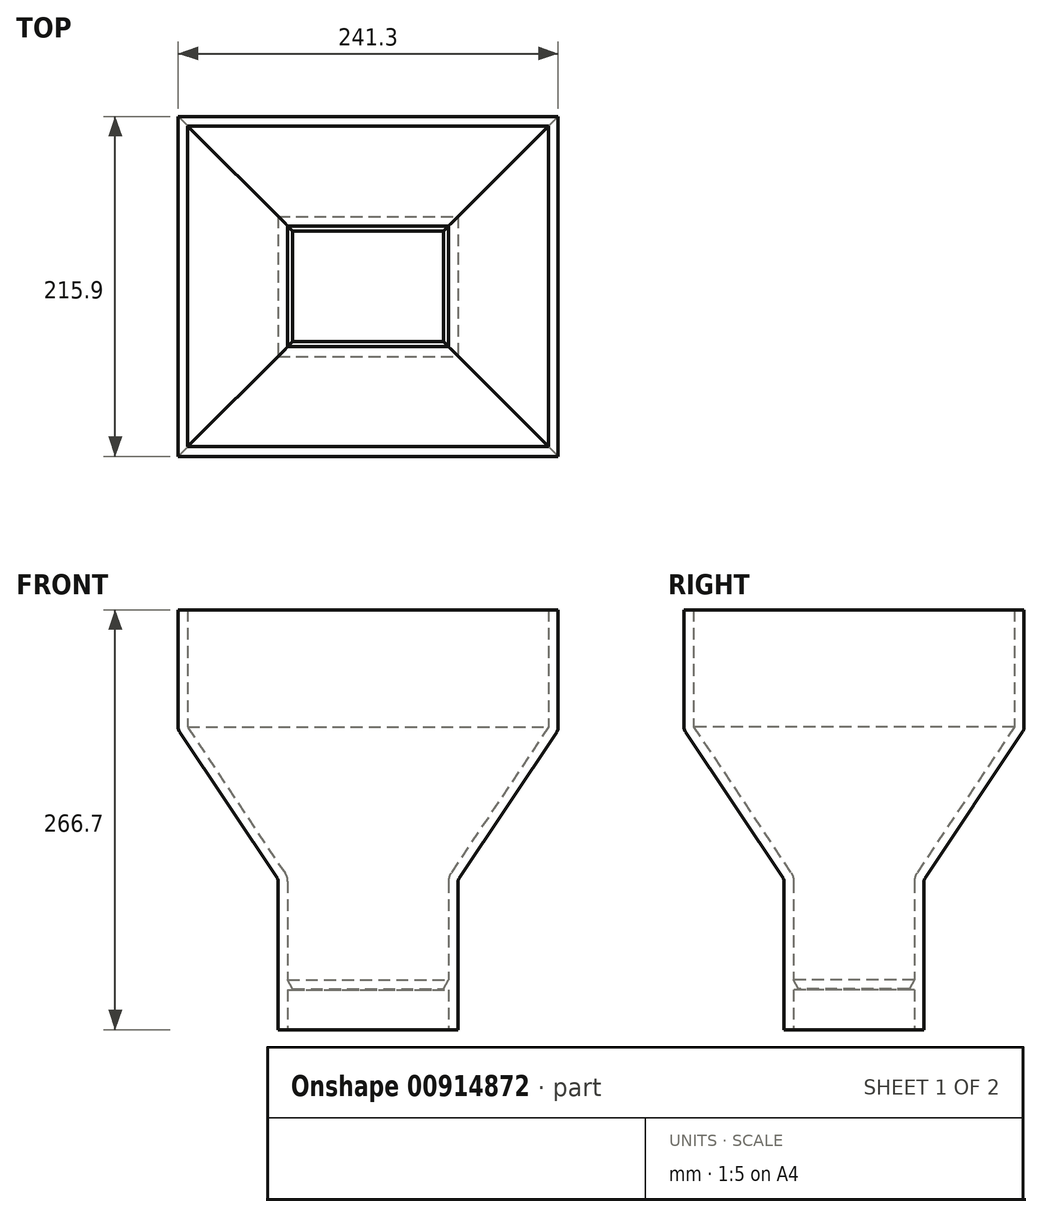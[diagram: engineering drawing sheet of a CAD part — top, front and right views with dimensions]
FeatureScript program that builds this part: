
annotation { "Feature Type Name" : "Feature", "Feature Type Description" : "" }
export const myFeature = defineFeature(function(context is Context, id is Id, definition is map)
    precondition{}
    {
        {
            var Q0;
            Q0=qCreatedBy(makeId("Top.planeOp"),FACE);
            var sketch = newSketch(context, id + "F0", { "sketchPlane" : qUnion([Q0])});
            skLineSegment(sketch, "E0.bottom", {"start": v(-39.4, 42.5) * mm, "end": v(74.9, 42.5) * mm});
            skLineSegment(sketch, "E0.top", {"start": v(-39.4, -46.4) * mm, "end": v(74.9, -46.4) * mm});
            skLineSegment(sketch, "E0.left", {"start": v(-39.4, 42.5) * mm, "end": v(-39.4, -46.4) * mm});
            skLineSegment(sketch, "E0.right", {"start": v(74.9, 42.5) * mm, "end": v(74.9, -46.4) * mm});
            skSolve(sketch);
        }
        {
            var Q0;
            Q0=makeQuery(id+"F0.imprint","IMPRINT",FACE,{"disambiguationData":[TD([[makeQuery(id+"F0.imprint","IMPRINT",EDGE,{"derivedFrom":sQuery(id+"F0.wireOp",EDGE,"E0.bottom")}),-1.0]])]});
            extrude(context, id + "F1", {"entities" : qUnion([Q0]), "depth" : 38.1 * mm, "offsetDistance" : 25.4 * mm});
        }
        {
            var Q0;
            Q0=makeQuery(id+"F1.opExtrude","CAP_FACE",FACE,{"disambiguationData":[OSD([sQuery(id+"F0.wireOp",EDGE,"E0.bottom"),sQuery(id+"F0.wireOp",EDGE,"E0.top"),sQuery(id+"F0.wireOp",EDGE,"E0.left"),sQuery(id+"F0.wireOp",EDGE,"E0.right")])],"isStart":false});
            var sketch = newSketch(context, id + "F2", { "sketchPlane" : qUnion([Q0])});
            skLineSegment(sketch, "E1.0.0", {"start": v(-39.4, 42.5) * mm, "end": v(-39.4, -46.4) * mm});
            skLineSegment(sketch, "E1.0.1", {"start": v(-39.4, -46.4) * mm, "end": v(74.9, -46.4) * mm});
            skLineSegment(sketch, "E1.0.2", {"start": v(74.9, -46.4) * mm, "end": v(74.9, 42.5) * mm});
            skLineSegment(sketch, "E1.0.3", {"start": v(74.9, 42.5) * mm, "end": v(-39.4, 42.5) * mm});
            skLineSegment(sketch, "E2.0", {"start": v(-102.9, 106) * mm, "end": v(-102.9, -109.9) * mm});
            skLineSegment(sketch, "E2.1", {"start": v(138.4, 106) * mm, "end": v(-102.9, 106) * mm});
            skLineSegment(sketch, "E2.2", {"start": v(138.4, -109.9) * mm, "end": v(138.4, 106) * mm});
            skLineSegment(sketch, "E2.3", {"start": v(-102.9, -109.9) * mm, "end": v(138.4, -109.9) * mm});
            skSolve(sketch);
        }
        {
            var Q0;
            Q0=makeQuery(id+"F2.imprint","IMPRINT",FACE,{"disambiguationData":[TD([[makeQuery(id+"F2.imprint","IMPRINT",EDGE,{"derivedFrom":sQuery(id+"F2.wireOp",EDGE,"E1.0.0")}),-1.0]])]});
            var Q1;
            Q1=makeQuery(id+"F2.imprint","IMPRINT",FACE,{"disambiguationData":[TD([[makeQuery(id+"F2.imprint","IMPRINT",EDGE,{"derivedFrom":sQuery(id+"F2.wireOp",EDGE,"E1.0.0")}),1.0]])]});
            extrude(context, id + "F3", {"entities" : qUnion([Q0, Q1]), "operationType" : NewBodyOperationType.ADD, "depth" : 152.4 * mm, "offsetDistance" : 25.4 * mm});
        }
        {
            var Q0;
            Q0=makeQuery(id+"F3.opExtrude","CAP_EDGE",EDGE,{"disambiguationData":[OSD([sQuery(id+"F2.wireOp",EDGE,"E2.3")])],"isStart":true});
            var Q1;
            Q1=makeQuery(id+"F3.opExtrude","CAP_EDGE",EDGE,{"disambiguationData":[OSD([sQuery(id+"F2.wireOp",EDGE,"E2.0")])],"isStart":true});
            var Q2;
            Q2=makeQuery(id+"F3.opExtrude","CAP_EDGE",EDGE,{"disambiguationData":[OSD([sQuery(id+"F2.wireOp",EDGE,"E2.2")])],"isStart":true});
            var Q3;
            Q3=makeQuery(id+"F3.opExtrude","CAP_EDGE",EDGE,{"disambiguationData":[OSD([sQuery(id+"F2.wireOp",EDGE,"E2.1")])],"isStart":true});
            chamfer(context, id + "F4", {"entities" : qUnion([Q0, Q1, Q2, Q3]), "chamferType" : ChamferType.TWO_OFFSETS, "width1" : 152.4 * mm, "oppositeDirection" : false, "width2" : 101.6 * mm, "tangentPropagation" : true});
        }
        {
            var Q0;
            Q0=makeQuery(id+"F3.opExtrude","CAP_FACE",FACE,{"disambiguationData":[OSD([sQuery(id+"F2.wireOp",EDGE,"E2.0"),sQuery(id+"F2.wireOp",EDGE,"E2.1"),sQuery(id+"F2.wireOp",EDGE,"E2.2"),sQuery(id+"F2.wireOp",EDGE,"E2.3")])],"isStart":false});
            var sketch = newSketch(context, id + "F5", { "sketchPlane" : qUnion([Q0])});
            skLineSegment(sketch, "E3.0.0", {"start": v(-102.9, 106) * mm, "end": v(-102.9, -109.9) * mm});
            skLineSegment(sketch, "E3.0.1", {"start": v(-102.9, -109.9) * mm, "end": v(138.4, -109.9) * mm});
            skLineSegment(sketch, "E3.0.2", {"start": v(138.4, -109.9) * mm, "end": v(138.4, 106) * mm});
            skLineSegment(sketch, "E3.0.3", {"start": v(138.4, 106) * mm, "end": v(-102.9, 106) * mm});
            skSolve(sketch);
        }
        {
            var Q0;
            Q0=makeQuery(id+"F5.imprint","IMPRINT",FACE,{"disambiguationData":[TD([[makeQuery(id+"F5.imprint","IMPRINT",EDGE,{"derivedFrom":sQuery(id+"F5.wireOp",EDGE,"E3.0.0")}),1.0]])]});
            extrude(context, id + "F6", {"entities" : qUnion([Q0]), "operationType" : NewBodyOperationType.ADD, "depth" : 76.2 * mm, "offsetDistance" : 25.4 * mm});
        }
        {
            var Q0;
            Q0=makeQuery(id+"F4.opChamfer","BLEND_EDGE",EDGE,{"blendedFrom":[makeQuery(id+"F3.opExtrude","CAP_EDGE",EDGE,{"disambiguationData":[OSD([sQuery(id+"F2.wireOp",EDGE,"E2.2")])],"isStart":true}),makeQuery(id+"F1.opExtrude","SWEPT_FACE",FACE,{"disambiguationData":[OSD([sQuery(id+"F0.wireOp",EDGE,"E0.right")])]})],"blendedInto":[makeQuery(id+"F1.opExtrude","SWEPT_FACE",FACE,{"disambiguationData":[OSD([sQuery(id+"F0.wireOp",EDGE,"E0.right")])]})]});
            var Q1;
            Q1=makeQuery(id+"F4.opChamfer","BLEND_EDGE",EDGE,{"blendedFrom":[makeQuery(id+"F3.opExtrude","CAP_EDGE",EDGE,{"disambiguationData":[OSD([sQuery(id+"F2.wireOp",EDGE,"E2.3")])],"isStart":true}),makeQuery(id+"F1.opExtrude","SWEPT_FACE",FACE,{"disambiguationData":[OSD([sQuery(id+"F0.wireOp",EDGE,"E0.top")])]})],"blendedInto":[makeQuery(id+"F1.opExtrude","SWEPT_FACE",FACE,{"disambiguationData":[OSD([sQuery(id+"F0.wireOp",EDGE,"E0.top")])]})]});
            var Q2;
            Q2=makeQuery(id+"F4.opChamfer","BLEND_EDGE",EDGE,{"blendedFrom":[makeQuery(id+"F3.opExtrude","CAP_EDGE",EDGE,{"disambiguationData":[OSD([sQuery(id+"F2.wireOp",EDGE,"E2.0")])],"isStart":true}),makeQuery(id+"F1.opExtrude","SWEPT_FACE",FACE,{"disambiguationData":[OSD([sQuery(id+"F0.wireOp",EDGE,"E0.left")])]})],"blendedInto":[makeQuery(id+"F1.opExtrude","SWEPT_FACE",FACE,{"disambiguationData":[OSD([sQuery(id+"F0.wireOp",EDGE,"E0.left")])]})]});
            var Q3;
            Q3=makeQuery(id+"F4.opChamfer","BLEND_EDGE",EDGE,{"blendedFrom":[makeQuery(id+"F3.opExtrude","CAP_EDGE",EDGE,{"disambiguationData":[OSD([sQuery(id+"F2.wireOp",EDGE,"E2.1")])],"isStart":true}),makeQuery(id+"F1.opExtrude","SWEPT_FACE",FACE,{"disambiguationData":[OSD([sQuery(id+"F0.wireOp",EDGE,"E0.bottom")])]})],"blendedInto":[makeQuery(id+"F1.opExtrude","SWEPT_FACE",FACE,{"disambiguationData":[OSD([sQuery(id+"F0.wireOp",EDGE,"E0.bottom")])]})]});
            fillet(context, id + "F7", {"entities" : qUnion([Q0, Q1, Q2, Q3]), "radius" : 3.17 * mm, "tangentPropagation" : true, "allowEdgeOverflow" : false});
        }
        {
            var Q0;
            {var subQ0=sQuery(id+"F2.wireOp",EDGE,"E2.2");Q0=makeQuery(id+"F6.boolean.opBoolean","MERGE",EDGE,{"derivedFrom":[makeQuery(id+"F4.opChamfer","BLEND_EDGE",EDGE,{"blendedFrom":[makeQuery(id+"F3.opExtrude","CAP_EDGE",EDGE,{"disambiguationData":[OSD([subQ0])],"isStart":true}),makeQuery(id+"F3.opExtrude","CAP_FACE",FACE,{"disambiguationData":[OSD([sQuery(id+"F2.wireOp",EDGE,"E2.0"),sQuery(id+"F2.wireOp",EDGE,"E2.1"),subQ0,sQuery(id+"F2.wireOp",EDGE,"E2.3")])],"isStart":false})],"blendedInto":[makeQuery(id+"F3.opExtrude","CAP_FACE",FACE,{"disambiguationData":[OSD([sQuery(id+"F2.wireOp",EDGE,"E2.0"),sQuery(id+"F2.wireOp",EDGE,"E2.1"),subQ0,sQuery(id+"F2.wireOp",EDGE,"E2.3")])],"isStart":false})]}),makeQuery(id+"F6.opExtrude","CAP_EDGE",EDGE,{"disambiguationData":[OSD([sQuery(id+"F5.wireOp",EDGE,"E3.0.2")])],"isStart":true})]});}
            var Q1;
            {var subQ0=sQuery(id+"F2.wireOp",EDGE,"E2.1");Q1=makeQuery(id+"F6.boolean.opBoolean","MERGE",EDGE,{"derivedFrom":[makeQuery(id+"F4.opChamfer","BLEND_EDGE",EDGE,{"blendedFrom":[makeQuery(id+"F3.opExtrude","CAP_EDGE",EDGE,{"disambiguationData":[OSD([subQ0])],"isStart":true}),makeQuery(id+"F3.opExtrude","CAP_FACE",FACE,{"disambiguationData":[OSD([sQuery(id+"F2.wireOp",EDGE,"E2.0"),subQ0,sQuery(id+"F2.wireOp",EDGE,"E2.2"),sQuery(id+"F2.wireOp",EDGE,"E2.3")])],"isStart":false})],"blendedInto":[makeQuery(id+"F3.opExtrude","CAP_FACE",FACE,{"disambiguationData":[OSD([sQuery(id+"F2.wireOp",EDGE,"E2.0"),subQ0,sQuery(id+"F2.wireOp",EDGE,"E2.2"),sQuery(id+"F2.wireOp",EDGE,"E2.3")])],"isStart":false})]}),makeQuery(id+"F6.opExtrude","CAP_EDGE",EDGE,{"disambiguationData":[OSD([sQuery(id+"F5.wireOp",EDGE,"E3.0.3")])],"isStart":true})]});}
            var Q2;
            {var subQ0=sQuery(id+"F2.wireOp",EDGE,"E2.0");Q2=makeQuery(id+"F6.boolean.opBoolean","MERGE",EDGE,{"derivedFrom":[makeQuery(id+"F4.opChamfer","BLEND_EDGE",EDGE,{"blendedFrom":[makeQuery(id+"F3.opExtrude","CAP_EDGE",EDGE,{"disambiguationData":[OSD([subQ0])],"isStart":true}),makeQuery(id+"F3.opExtrude","CAP_FACE",FACE,{"disambiguationData":[OSD([subQ0,sQuery(id+"F2.wireOp",EDGE,"E2.1"),sQuery(id+"F2.wireOp",EDGE,"E2.2"),sQuery(id+"F2.wireOp",EDGE,"E2.3")])],"isStart":false})],"blendedInto":[makeQuery(id+"F3.opExtrude","CAP_FACE",FACE,{"disambiguationData":[OSD([subQ0,sQuery(id+"F2.wireOp",EDGE,"E2.1"),sQuery(id+"F2.wireOp",EDGE,"E2.2"),sQuery(id+"F2.wireOp",EDGE,"E2.3")])],"isStart":false})]}),makeQuery(id+"F6.opExtrude","CAP_EDGE",EDGE,{"disambiguationData":[OSD([sQuery(id+"F5.wireOp",EDGE,"E3.0.0")])],"isStart":true})]});}
            var Q3;
            {var subQ0=sQuery(id+"F2.wireOp",EDGE,"E2.3");Q3=makeQuery(id+"F6.boolean.opBoolean","MERGE",EDGE,{"derivedFrom":[makeQuery(id+"F4.opChamfer","BLEND_EDGE",EDGE,{"blendedFrom":[makeQuery(id+"F3.opExtrude","CAP_EDGE",EDGE,{"disambiguationData":[OSD([subQ0])],"isStart":true}),makeQuery(id+"F3.opExtrude","CAP_FACE",FACE,{"disambiguationData":[OSD([sQuery(id+"F2.wireOp",EDGE,"E2.0"),sQuery(id+"F2.wireOp",EDGE,"E2.1"),sQuery(id+"F2.wireOp",EDGE,"E2.2"),subQ0])],"isStart":false})],"blendedInto":[makeQuery(id+"F3.opExtrude","CAP_FACE",FACE,{"disambiguationData":[OSD([sQuery(id+"F2.wireOp",EDGE,"E2.0"),sQuery(id+"F2.wireOp",EDGE,"E2.1"),sQuery(id+"F2.wireOp",EDGE,"E2.2"),subQ0])],"isStart":false})]}),makeQuery(id+"F6.opExtrude","CAP_EDGE",EDGE,{"disambiguationData":[OSD([sQuery(id+"F5.wireOp",EDGE,"E3.0.1")])],"isStart":true})]});}
            fillet(context, id + "F8", {"entities" : qUnion([Q0, Q1, Q2, Q3]), "radius" : 5.08 * mm, "tangentPropagation" : true, "allowEdgeOverflow" : false});
        }
        {
            var Q0;
            Q0=makeQuery(id+"F6.opExtrude","CAP_FACE",FACE,{"disambiguationData":[OSD([sQuery(id+"F5.wireOp",EDGE,"E3.0.0"),sQuery(id+"F5.wireOp",EDGE,"E3.0.1"),sQuery(id+"F5.wireOp",EDGE,"E3.0.2"),sQuery(id+"F5.wireOp",EDGE,"E3.0.3")])],"isStart":false});
            var Q1;
            Q1=makeQuery(id+"F1.opExtrude","CAP_FACE",FACE,{"disambiguationData":[OSD([sQuery(id+"F0.wireOp",EDGE,"E0.bottom"),sQuery(id+"F0.wireOp",EDGE,"E0.top"),sQuery(id+"F0.wireOp",EDGE,"E0.left"),sQuery(id+"F0.wireOp",EDGE,"E0.right")])],"isStart":true});
            shell(context, id + "F9", {"entities" : qUnion([Q0, Q1]), "thickness" : 6.1 * mm});
        }
        {
            var Q0;
            Q0=qCreatedBy(makeId("Top.planeOp"),FACE);
            cPlane(context, id + "F10", {"entities" : qUnion([Q0]), "cplaneType" : CPlaneType.OFFSET, "offset" : 25.4 * mm, "width" : 152.4 * mm, "height" : 152.4 * mm});
        }
        {
            var Q0;
            Q0=qCreatedBy(id+"F10.planeOp",FACE);
            var sketch = newSketch(context, id + "F11", { "sketchPlane" : qUnion([Q0])});
            skLineSegment(sketch, "E4.0.0", {"start": v(-39.4, -46.4) * mm, "end": v(-39.4, 42.5) * mm});
            skLineSegment(sketch, "E4.0.1", {"start": v(-39.4, 42.5) * mm, "end": v(74.9, 42.5) * mm});
            skLineSegment(sketch, "E4.0.2", {"start": v(74.9, 42.5) * mm, "end": v(74.9, -46.4) * mm});
            skLineSegment(sketch, "E4.0.3", {"start": v(74.9, -46.4) * mm, "end": v(-39.4, -46.4) * mm});
            skLineSegment(sketch, "E5.0", {"start": v(-33.31, -40.31) * mm, "end": v(68.8, -40.31) * mm});
            skLineSegment(sketch, "E6.0", {"start": v(-33.31, 36.4) * mm, "end": v(-33.31, -40.31) * mm});
            skLineSegment(sketch, "E7.0", {"start": v(-33.31, 36.4) * mm, "end": v(68.8, 36.4) * mm});
            skLineSegment(sketch, "E8.0", {"start": v(68.8, 36.4) * mm, "end": v(68.8, -40.31) * mm});
            skLineSegment(sketch, "E9.0", {"start": v(-30.14, -37.14) * mm, "end": v(65.62, -37.14) * mm});
            skLineSegment(sketch, "E9.1", {"start": v(-30.14, 33.22) * mm, "end": v(-30.14, -37.14) * mm});
            skLineSegment(sketch, "E9.2", {"start": v(-30.14, 33.22) * mm, "end": v(65.62, 33.22) * mm});
            skLineSegment(sketch, "E9.3", {"start": v(65.62, 33.22) * mm, "end": v(65.62, -37.14) * mm});
            skSolve(sketch);
        }
        {
            var Q0;
            Q0=makeQuery(id+"F11.imprint","IMPRINT",FACE,{"disambiguationData":[TD([[makeQuery(id+"F11.imprint","IMPRINT",EDGE,{"derivedFrom":sQuery(id+"F11.wireOp",EDGE,"E5.0")}),1.0]])]});
            extrude(context, id + "F12", {"entities" : qUnion([Q0]), "operationType" : NewBodyOperationType.ADD, "depth" : 6.35 * mm, "offsetDistance" : 25.4 * mm});
        }
        {
            var Q0;
            Q0=makeQuery(id+"F12.opExtrude","CAP_EDGE",EDGE,{"disambiguationData":[OSD([sQuery(id+"F11.wireOp",EDGE,"E9.0")])],"isStart":false});
            var Q1;
            Q1=makeQuery(id+"F12.opExtrude","CAP_EDGE",EDGE,{"disambiguationData":[OSD([sQuery(id+"F11.wireOp",EDGE,"E9.1")])],"isStart":false});
            var Q2;
            Q2=makeQuery(id+"F12.opExtrude","CAP_EDGE",EDGE,{"disambiguationData":[OSD([sQuery(id+"F11.wireOp",EDGE,"E9.3")])],"isStart":false});
            var Q3;
            Q3=makeQuery(id+"F12.opExtrude","CAP_EDGE",EDGE,{"disambiguationData":[OSD([sQuery(id+"F11.wireOp",EDGE,"E9.2")])],"isStart":false});
            chamfer(context, id + "F13", {"entities" : qUnion([Q0, Q1, Q2, Q3]), "chamferType" : ChamferType.TWO_OFFSETS, "width1" : 5.7 * mm, "oppositeDirection" : false, "width2" : 3.17 * mm, "tangentPropagation" : true});
        }
    });
